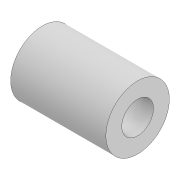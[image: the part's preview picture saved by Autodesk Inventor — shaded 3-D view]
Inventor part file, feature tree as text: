
AUTODESK INVENTOR PART (.ipt)
format: ipt  version: 2022 (Build 260153000, 153)  size: 83,968 bytes
history: native  units: mm
features: extrude x1, sketch x1
ambient origin geometry x8: Origin, YZ Plane, XZ Plane, XY Plane, X Axis, Y Axis, Z Axis, Center Point
bodies: Solid1 (feature_tree)
feature tree (2):
  extrude  "Extrusion1"  Depth=2.0mm
  sketch  "Sketch1"  dims[d0=4.0mm d1=2.0mm d2=6.0mm d3=0.0mm]
